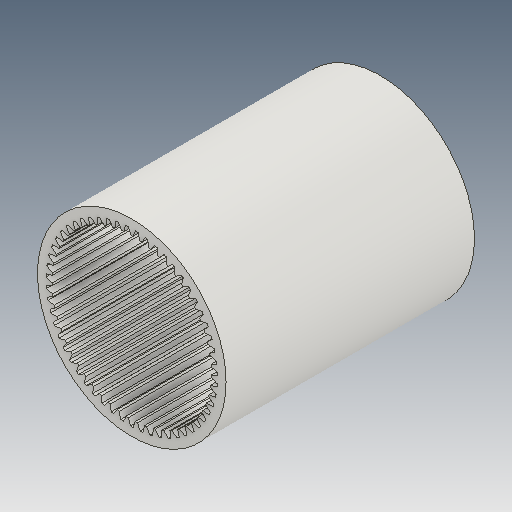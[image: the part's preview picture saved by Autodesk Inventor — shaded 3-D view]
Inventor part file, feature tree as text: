
AUTODESK INVENTOR PART (.ipt)
format: ipt  version: 2020.3 (Build 243373010, 373A)  size: 420,864 bytes
history: native  units: mm (DEFAULTED — no unit token found)
features: plane x3, other x3, sketch x2, extrude x1
ambient origin geometry x8: Origin, YZ Plane, XZ Plane, XY Plane, X Axis, Y Axis, Z Axis, Center Point
bodies: Solid1 (feature_tree)
feature tree (9):
  extrude  "Extrusion1"  Depth=35.0mm TaperAngle=0.0deg
  plane  "Work Plane2"
  plane  "Work Plane8"
  plane  "Work Plane9"
  other  "Spur Gear"
  sketch  "Sketch1"  dims[d0=26.565mm d1=35.0mm d2=0.0mm]
  sketch  "Sketch2"  dims[d3=23.1mm d4=10.0mm d5=0.0mm d16=8.4mm d17=0.0mm d34=0.571199mm d39=0.0mm d45=0.0mm d47=8.4mm d50=0.0mm d51=0.0mm d52=8.4mm]
  other  "Srf1"
  other  "Pitch Diameter"
